# Revit family: STS-409К_RV17_LOD_400
name_source: partatom
category: Электрооборудование
revit_build: Autodesk Revit 2017 (Build: 20170118_1100(x64)
units: mm (PartAtom-declared; Revit-internal decimal feet)

## family parameters
Всегда вертикально = Да
Конфигурация панели = Два столбца, слева направо
На основе рабочей плоскости = Нет
Общий = Нет
При загрузке вырезать с полостями = Нет
Размер круглого соединителя = Использовать диаметр
Тип детали = Щит
Точка расчета площади = Нет

## types (1)
- STS-409K
    ADSK_URL страницы изделия = https://stilsoft.ru
    ADSK_Единица измерения = шт.
    ADSK_Завод-изготовитель = ООО «Основа Безопасности»
    ADSK_Количество = 1
    ADSK_Марка = СТАЕ.426469.033-01
    ADSK_Масса = 1.8
    ADSK_Наименование = STS-409К
    ADSK_Размер_Высота = 278 мм
    ADSK_Размер_Глубина = 84 мм
    ADSK_Размер_Ширина = 293 мм
    Диапазон рабочих температур, °С = от +5 до +50
    Длина кода ключа (пропуска), символов = 1-8
    Интерфейс считывателей (1) = Wiegand 26
    Интерфейс считывателей (2) = Wiegand 40/42
    Информационная ёмкость (количество ШС) = 8
    Количество подключаемых считывающих устройств, не более, шт. = 2
    Количество реле, шт. = 4
    Максимальное время работы в автономном режиме, ч = 24
    Максимальное количество извещателей ОПС на 1 шлейф сигнализации, не более, шт. = 20
    Максимальное количество пропусков ОПС, шт. = 15
    Максимальное удаление считывающих устройств от контролера, не более, м = 100 мм
    Максимальный потребляемый контроллером ток от сети переменного тока (без дополнительных внешних потребителей), А = 0 А
    Максимальный ток, проходящий через реле, не более, А (для 220В) = 2 А
    Максимальный ток, проходящий через реле, не более, А (для 24В и 12В) = 4 А
    Напряжение = 220
    Напряжение электропитания в автономном режиме, В = 12
    Предельное значение сопротивления проводов ШС, кОм = 0.1
    Стандарт интерфейса связи = 10 Base-T Ethernet (гнездо RJ-45)
    Частота переменного однофазного тока, Гц = 50 Гц
